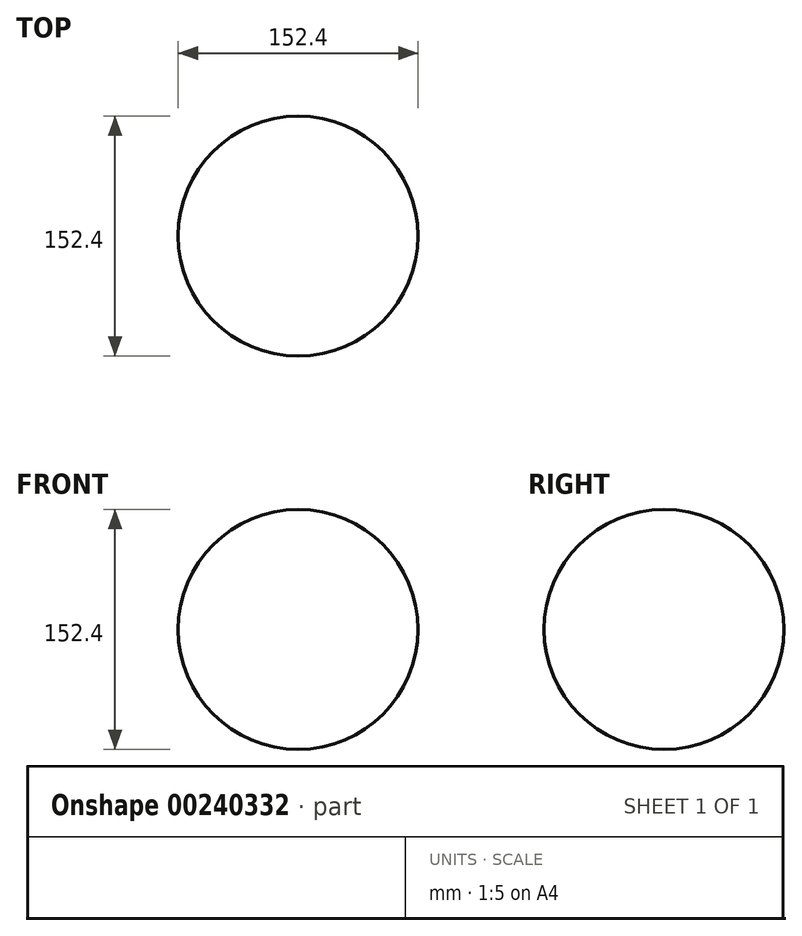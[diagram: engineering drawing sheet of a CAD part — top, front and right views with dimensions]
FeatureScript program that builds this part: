
annotation { "Feature Type Name" : "Feature", "Feature Type Description" : "" }
export const myFeature = defineFeature(function(context is Context, id is Id, definition is map)
    precondition{}
    {
        {
            var Q0;
            Q0=qCreatedBy(makeId("Front.planeOp"),FACE);
            var sketch = newSketch(context, id + "F0", { "sketchPlane" : qUnion([Q0])});
            skCircle(sketch, "E0", {"center": v(0, 0) * mm, "radius": 76.2 * mm});
            skSolve(sketch);
        }
        {
            var Q0;
            Q0=makeQuery(id+"F0.imprint","IMPRINT",FACE,{"disambiguationData":[TD([[makeQuery(id+"F0.imprint","IMPRINT",EDGE,{"derivedFrom":sQuery(id+"F0.wireOp",EDGE,"E0")}),1.0]])]});
            extrude(context, id + "F1", {"entities" : qUnion([Q0]), "endBound" : BoundingType.SYMMETRIC, "depth" : 152.4 * mm});
        }
        {
            var Q0;
            Q0=makeQuery(id+"F1.opExtrude","CAP_EDGE",EDGE,{"disambiguationData":[OSD([sQuery(id+"F0.wireOp",EDGE,"E0")])],"isStart":false});
            fillet(context, id + "F2", {"entities" : qUnion([Q0]), "radius" : 76.2 * mm, "tangentPropagation" : true, "allowEdgeOverflow" : false});
        }
        {
            var Q0;
            Q0=makeQuery(id+"F1.opExtrude","CAP_EDGE",EDGE,{"disambiguationData":[OSD([sQuery(id+"F0.wireOp",EDGE,"E0")])],"isStart":true});
            fillet(context, id + "F3", {"entities" : qUnion([Q0]), "radius" : 76.2 * mm, "tangentPropagation" : true, "allowEdgeOverflow" : false});
        }
    });
